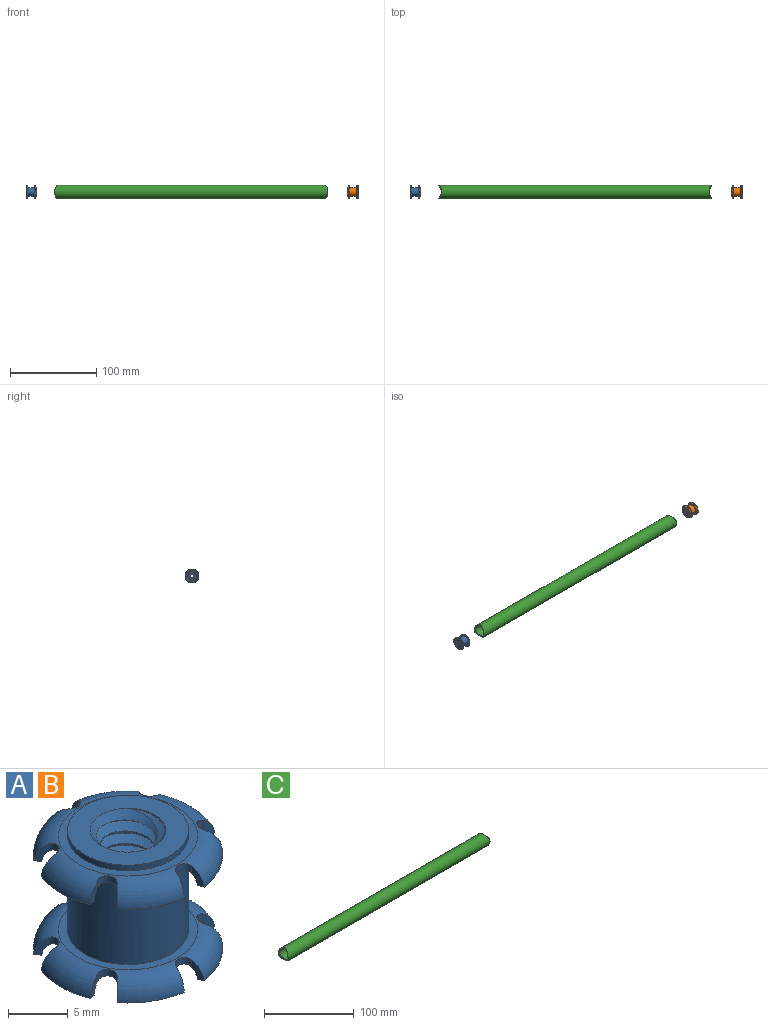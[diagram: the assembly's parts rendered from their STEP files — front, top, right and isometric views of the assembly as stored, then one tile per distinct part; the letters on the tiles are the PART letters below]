
ASSEMBLY  parts=3 mates=2
PART A: 67 faces, bbox 17.3x17.3x12.8 mm
  f0: cylinder r=0.88mm len=1.51mm, axis (0,0,1), area 1.6mm2, adj f8,f9,f65,f66
  f1: cylinder r=0.88mm len=1.51mm, axis (0,0,1), area 1.6mm2, adj f6,f7,f63,f64
  f2: cylinder r=0.88mm len=1.51mm, axis (0,0,1), area 1.6mm2, adj f8,f9,f43,f44
  f3: cylinder r=0.88mm len=1.51mm, axis (0,0,1), area 1.6mm2, adj f6,f7,f41,f42
  f4: cylinder r=0.88mm len=1.7mm, axis (0,0,1), area 1.6mm2, adj f8,f9,f39,f40
  f5: cylinder r=0.88mm len=1.7mm, axis (0,0,1), area 1.6mm2, adj f6,f7,f37,f38
  f6: torus R=5.84mm, axis (0,0,-1), area 71.2mm2, adj f1,f3,f5,f18,f20,f22,f24,f26
  f7: torus R=5.84mm, axis (0,0,-1), area 107.1mm2, adj f1,f3,f5,f18,f20,f22,f24,f26
  f8: torus R=5.84mm, axis (0,0,-1), area 71.2mm2, adj f0,f2,f4,f17,f19,f21,f23,f25
  f9: torus R=5.84mm, axis (0,0,-1), area 107.1mm2, adj f0,f2,f4,f17,f19,f21,f23,f25
  f10: cone r=3.17mm half-angle=45deg, axis (0,0,1), area 10.5mm2, adj f16,f27,f28,f30
  f11: cone r=3.17mm half-angle=45deg, axis (0,0,-1), area 10.5mm2, adj f16,f27,f28,f29
  f12: cylinder r=5.08mm len=10.16mm, axis (0,0,-1), area 18.2mm2, adj f29,f35
  f13: cylinder r=5.08mm len=10.16mm, axis (0,0,-1), area 286.2mm2, adj f32,f34
  f14: cylinder r=5.08mm len=10.16mm, axis (0,0,-1), area 18.2mm2, adj f30,f31
  f15: cylinder r=3.17mm len=11.43mm, axis (0,0,-1), area 28.5mm2, adj f27,f28,f29,f30
  f16: cylinder r=2.35mm len=9.78mm, axis (0,0,-1), area 18mm2, adj f10,f11,f27,f28
  f17: cone r=7.94mm half-angle=85.2deg, axis (0,0,1), area 3.8mm2, adj f8,f9,f62,f65
  f18: cone r=7.94mm half-angle=85.2deg, axis (0,0,1), area 3.8mm2, adj f6,f7,f58,f63
  f19: cone r=7.94mm half-angle=85.2deg, axis (0,0,1), area 3.8mm2, adj f8,f9,f56,f61
  f20: cone r=7.94mm half-angle=85.2deg, axis (0,0,1), area 3.8mm2, adj f6,f7,f52,f57
  f21: cone r=7.94mm half-angle=85.2deg, axis (0,0,1), area 3.8mm2, adj f8,f9,f50,f55
  f22: cone r=7.94mm half-angle=85.2deg, axis (0,0,1), area 3.8mm2, adj f6,f7,f46,f51
  f23: cone r=7.94mm half-angle=85.2deg, axis (0,0,1), area 3.8mm2, adj f8,f9,f44,f49
  f24: cone r=7.94mm half-angle=85.2deg, axis (0,0,1), area 3.8mm2, adj f6,f7,f42,f45
  f25: cone r=7.94mm half-angle=85.2deg, axis (0,0,1), area 3.8mm2, adj f8,f9,f40,f43
  f26: cone r=7.94mm half-angle=85.2deg, axis (0,0,1), area 3.8mm2, adj f6,f7,f38,f41
  f27: bspline ~11.91x7.33mm, area 138.8mm2, adj f10,f11,f15,f16
  f28: bspline ~12.12x7.33mm, area 138.9mm2, adj f10,f11,f15,f16
  f29: plane 10.16x10.16mm, normal (0,0,-1), area 49.4mm2, adj f11,f12,f15
  f30: plane 10.16x10.16mm, normal (0,0,1), area 49.4mm2, adj f10,f14,f15
  f31: plane 11.68x11.68mm, normal (0,0,1), area 26.1mm2, adj f9,f14
  f32: plane 11.68x11.68mm, normal (0,0,-1), area 26.1mm2, adj f8,f13
  f33: cone r=7.94mm half-angle=85.2deg, axis (0,0,1), area 3.8mm2, adj f8,f9,f39,f66
  f34: plane 11.68x11.68mm, normal (0,0,1), area 26.1mm2, adj f7,f13
  f35: plane 11.68x11.68mm, normal (0,0,-1), area 26.1mm2, adj f6,f12
  f36: cone r=7.94mm half-angle=85.2deg, axis (0,0,1), area 3.8mm2, adj f6,f7,f37,f64
  f37: plane 1.86x1.26mm, normal (0.97,0.26,0), area 1.1mm2, adj f5,f6,f7,f36
  f38: plane 1.86x1.26mm, normal (-0.97,0.26,0), area 1.1mm2, adj f5,f6,f7,f26
  f39: plane 1.86x1.26mm, normal (0.97,0.26,0), area 1.1mm2, adj f4,f8,f9,f33
  f40: plane 1.86x1.26mm, normal (-0.97,0.26,0), area 1.1mm2, adj f4,f8,f9,f25
  f41: plane 1.86x0.94mm, normal (0.71,-0.71,0), area 1.1mm2, adj f3,f6,f7,f26
  f42: plane 1.86x1.26mm, normal (-0.26,0.97,0), area 1.1mm2, adj f3,f6,f7,f24
  f43: plane 1.86x0.94mm, normal (0.71,-0.71,0), area 1.1mm2, adj f2,f8,f9,f25
  f44: plane 1.86x1.26mm, normal (-0.26,0.97,0), area 1.1mm2, adj f2,f8,f9,f23
  f45: plane 1.86x1.26mm, normal (-0.26,-0.97,0), area 1.1mm2, adj f6,f7,f24,f47
  f46: plane 1.86x0.94mm, normal (0.71,0.71,0), area 1.1mm2, adj f6,f7,f22,f47
  f47: cylinder r=0.88mm len=1.51mm, axis (0,0,1), area 1.8mm2, adj f6,f7,f45,f46
  f48: cylinder r=0.88mm len=1.51mm, axis (0,0,1), area 1.8mm2, adj f8,f9,f49,f50
  f49: plane 1.86x1.26mm, normal (-0.26,-0.97,0), area 1.1mm2, adj f8,f9,f23,f48
  f50: plane 1.86x0.94mm, normal (0.71,0.71,0), area 1.1mm2, adj f8,f9,f21,f48
  f51: plane 1.86x1.26mm, normal (-0.97,-0.26,0), area 1.1mm2, adj f6,f7,f22,f53
  f52: plane 1.86x1.26mm, normal (0.97,-0.26,0), area 1.1mm2, adj f6,f7,f20,f53
  f53: cylinder r=0.88mm len=1.7mm, axis (0,0,1), area 1.6mm2, adj f6,f7,f51,f52
  f54: cylinder r=0.88mm len=1.7mm, axis (0,0,1), area 1.6mm2, adj f8,f9,f55,f56
  f55: plane 1.86x1.26mm, normal (-0.97,-0.26,0), area 1.1mm2, adj f8,f9,f21,f54
  f56: plane 1.86x1.26mm, normal (0.97,-0.26,0), area 1.1mm2, adj f8,f9,f19,f54
  f57: plane 1.86x0.94mm, normal (-0.71,0.71,0), area 1.1mm2, adj f6,f7,f20,f59
  f58: plane 1.86x1.26mm, normal (0.26,-0.97,0), area 1.1mm2, adj f6,f7,f18,f59
  f59: cylinder r=0.88mm len=1.51mm, axis (0,0,1), area 1.8mm2, adj f6,f7,f57,f58
  f60: cylinder r=0.88mm len=1.51mm, axis (0,0,1), area 1.8mm2, adj f8,f9,f61,f62
  f61: plane 1.86x0.94mm, normal (-0.71,0.71,0), area 1.1mm2, adj f8,f9,f19,f60
  f62: plane 1.86x1.26mm, normal (0.26,-0.97,0), area 1.1mm2, adj f8,f9,f17,f60
  f63: plane 1.86x1.26mm, normal (0.26,0.97,0), area 1.1mm2, adj f1,f6,f7,f18
  f64: plane 1.86x0.94mm, normal (-0.71,-0.71,0), area 1.1mm2, adj f1,f6,f7,f36
  f65: plane 1.86x1.26mm, normal (0.26,0.97,0), area 1.1mm2, adj f0,f8,f9,f17
  f66: plane 1.86x0.94mm, normal (-0.71,-0.71,0), area 1.1mm2, adj f0,f8,f9,f33
PART B: same geometry as A
PART C: 4 faces, bbox 317.8x17.8x17.8 mm
  f0: cylinder r=11.11mm len=17.81mm, axis (0,0.13,0.99), area 65.9mm2, adj f1,f2
  f1: cylinder r=7.94mm len=317.82mm, axis (1,0,0), area 15677.2mm2, adj f0,f3
  f2: cylinder r=6.69mm len=315.63mm, axis (1,0,0), area 13176.3mm2, adj f0,f3
  f3: cylinder r=11.11mm len=17.81mm, axis (0,0.13,0.99), area 65.8mm2, adj f1,f2
PLACE A rot(axis=(-0.69,0.24,-0.69),153.5deg) t=(-185.7,0,0)mm
PLACE B rot(axis=(-0.67,-0.3,0.67),146.7deg) t=(187.35,0,0)mm
PLACE C t=(0,260.09,-99.45)mm
MATE cylindrical B.f6 <-> C.f1  axis (1,0,0) through (193.07,0,0)mm
MATE cylindrical A.f6 <-> C.f1  axis (-1,0,0) through (-185.7,0,0)mm
